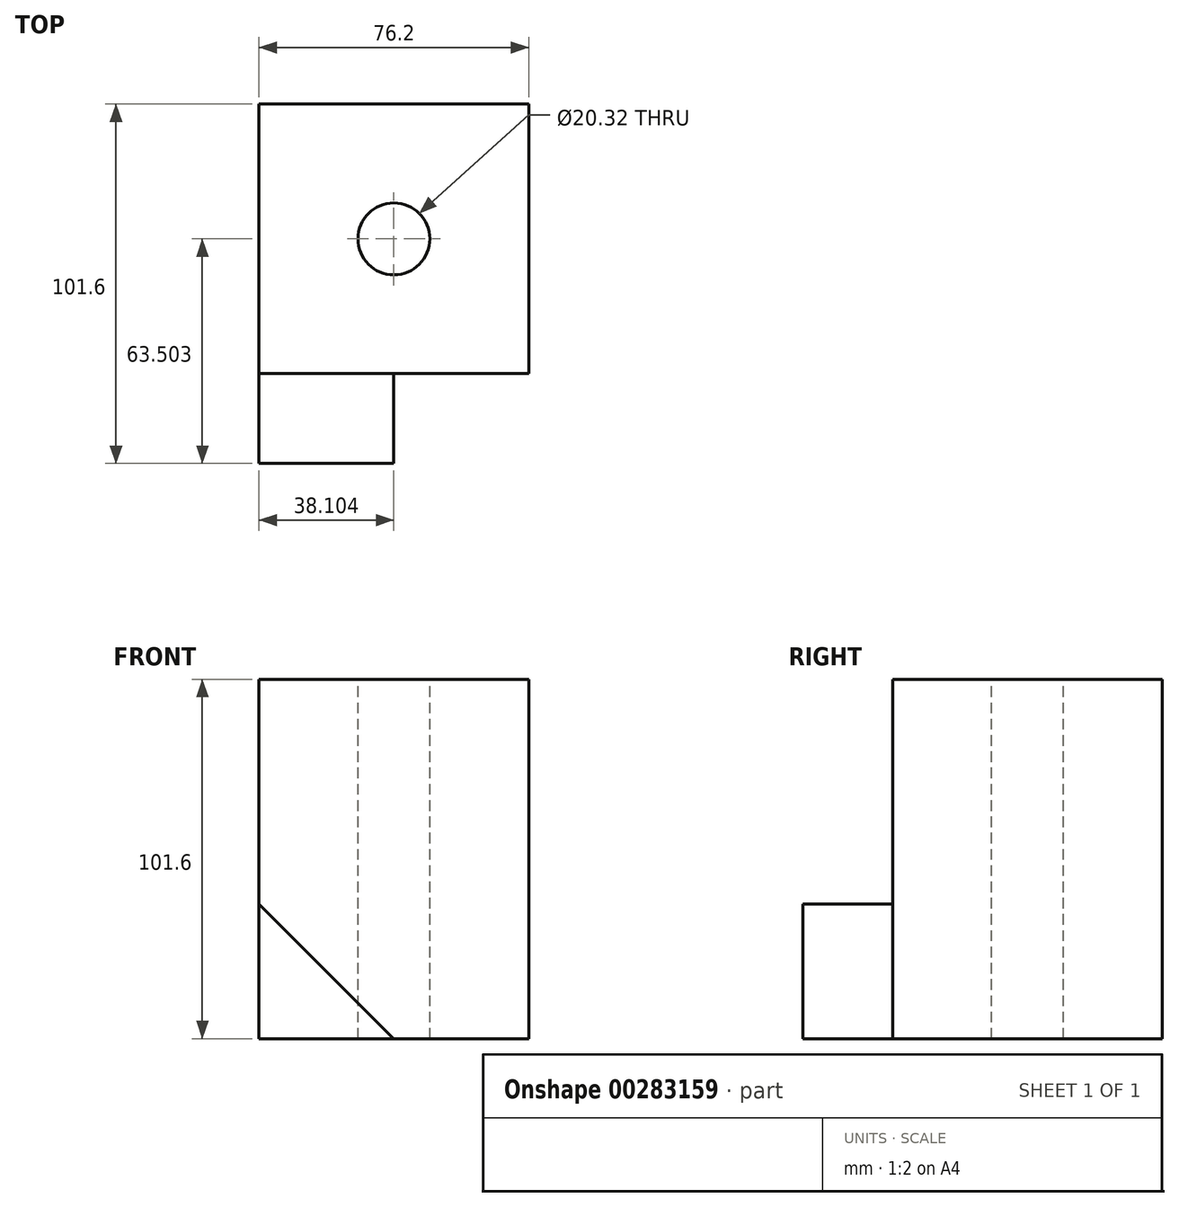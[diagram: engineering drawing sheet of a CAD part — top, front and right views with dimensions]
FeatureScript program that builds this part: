
annotation { "Feature Type Name" : "Feature", "Feature Type Description" : "" }
export const myFeature = defineFeature(function(context is Context, id is Id, definition is map)
    precondition{}
    {
        {
            var Q0;
            Q0=qCreatedBy(makeId("Top.planeOp"),FACE);
            var sketch = newSketch(context, id + "F0", { "sketchPlane" : qUnion([Q0])});
            skLineSegment(sketch, "E0.bottom", {"start": v(-35.12, 34.2) * mm, "end": v(41.08, 34.2) * mm});
            skLineSegment(sketch, "E0.top", {"start": v(-35.12, -42) * mm, "end": v(41.08, -42) * mm});
            skLineSegment(sketch, "E0.left", {"start": v(-35.12, 34.2) * mm, "end": v(-35.12, -42) * mm});
            skLineSegment(sketch, "E0.right", {"start": v(41.08, 34.2) * mm, "end": v(41.08, -42) * mm});
            skSolve(sketch);
        }
        {
            var Q0;
            Q0=makeQuery(id+"F0.imprint","IMPRINT",FACE,{"disambiguationData":[TD([[makeQuery(id+"F0.imprint","IMPRINT",EDGE,{"derivedFrom":sQuery(id+"F0.wireOp",EDGE,"E0.bottom")}),-1.0]])]});
            extrude(context, id + "F1", {"entities" : qUnion([Q0]), "depth" : 101.6 * mm});
        }
        {
            var Q0;
            Q0=makeQuery(id+"F1.opExtrude","SWEPT_FACE",FACE,{"disambiguationData":[OSD([sQuery(id+"F0.wireOp",EDGE,"E0.top")])]});
            var sketch = newSketch(context, id + "F2", { "sketchPlane" : qUnion([Q0])});
            skLineSegment(sketch, "E1", {"start": v(-35.12, 0) * mm, "end": v(-35.12, 38.1) * mm});
            skLineSegment(sketch, "E2", {"start": v(-35.12, 0) * mm, "end": v(2.98, 0) * mm});
            skLineSegment(sketch, "E3", {"start": v(2.98, 0) * mm, "end": v(-35.12, 38.1) * mm});
            skSolve(sketch);
        }
        {
            var Q0;
            Q0=makeQuery(id+"F2.imprint","IMPRINT",FACE,{"disambiguationData":[TD([[makeQuery(id+"F2.imprint","IMPRINT",EDGE,{"derivedFrom":sQuery(id+"F2.wireOp",EDGE,"E1")}),1.0]])]});
            extrude(context, id + "F3", {"entities" : qUnion([Q0]), "operationType" : NewBodyOperationType.ADD, "depth" : 25.4 * mm});
        }
        {
            var Q0;
            Q0=makeQuery(id+"F1.opExtrude","CAP_FACE",FACE,{"disambiguationData":[OSD([sQuery(id+"F0.wireOp",EDGE,"E0.bottom"),sQuery(id+"F0.wireOp",EDGE,"E0.top"),sQuery(id+"F0.wireOp",EDGE,"E0.left"),sQuery(id+"F0.wireOp",EDGE,"E0.right")])],"isStart":false});
            var sketch = newSketch(context, id + "F4", { "sketchPlane" : qUnion([Q0])});
            skLineSegment(sketch, "E4", {"start": v(2.98, -42) * mm, "end": v(2.98, 34.2) * mm});
            skLineSegment(sketch, "E5", {"start": v(41.08, -3.9) * mm, "end": v(2.98, -3.9) * mm});
            skLineSegment(sketch, "E6", {"start": v(2.98, -3.9) * mm, "end": v(-35.12, -3.9) * mm});
            skCircle(sketch, "E7", {"center": v(2.98, -3.9) * mm, "radius": 10.16 * mm});
            skSolve(sketch);
        }
        {
            var Q0;
            Q0=sQuery(id+"F4.wireOp",VERTEX,"E7.center");
            var Q1;
            Q1=makeQuery(id+"F1.opExtrude","SWEPT_BODY",BODY,{"disambiguationData":[OSD([sQuery(id+"F0.wireOp",EDGE,"E0.bottom"),sQuery(id+"F0.wireOp",EDGE,"E0.top"),sQuery(id+"F0.wireOp",EDGE,"E0.left"),sQuery(id+"F0.wireOp",EDGE,"E0.right")])]});
            hole(context, id + "F5", {"style" : HoleStyle.SIMPLE, "endStyle" : HoleEndStyle.THROUGH, "holeDiameter" : 20.32 * mm, "tappedDepth" : 12.7 * mm, "tapClearance" : 3, "locations" : qUnion([Q0]), "scope" : qUnion([Q1])});
        }
    });
